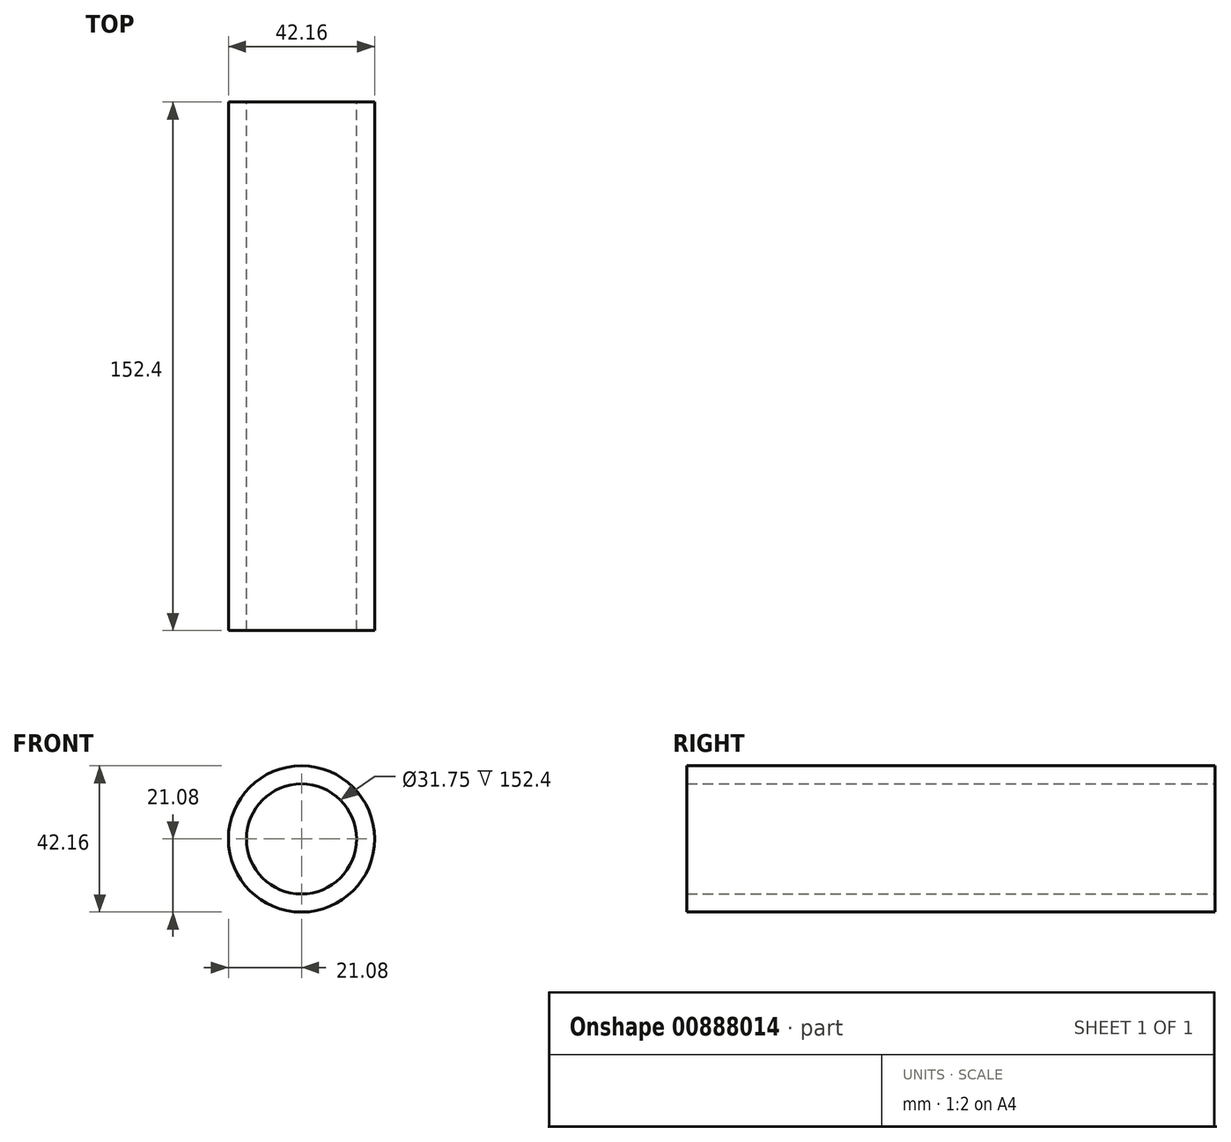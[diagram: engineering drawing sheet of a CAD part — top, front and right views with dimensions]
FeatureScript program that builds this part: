
annotation { "Feature Type Name" : "Feature", "Feature Type Description" : "" }
export const myFeature = defineFeature(function(context is Context, id is Id, definition is map)
    precondition{}
    {
        {
            var Q0;
            Q0=qCreatedBy(makeId("Front.planeOp"),FACE);
            var sketch = newSketch(context, id + "F0", { "sketchPlane" : qUnion([Q0])});
            skCircle(sketch, "E0", {"center": v(0, 0) * mm, "radius": 15.88 * mm});
            skCircle(sketch, "E1", {"center": v(0, 0) * mm, "radius": 21.08 * mm});
            skSolve(sketch);
        }
        {
            var Q0;
            Q0=makeQuery(id+"F0.imprint","IMPRINT",FACE,{"disambiguationData":[TD([[makeQuery(id+"F0.imprint","IMPRINT",EDGE,{"derivedFrom":sQuery(id+"F0.wireOp",EDGE,"E0")}),-1.0]])]});
            extrude(context, id + "F1", {"entities" : qUnion([Q0]), "depth" : 152.4 * mm, "offsetDistance" : 25.4 * mm});
        }
    });
